# Revit family: C2-260
name_source: partatom
category: Устройства связи
units: mm (PartAtom-declared; Revit-internal decimal feet)

## family parameters
Всегда вертикально = Нет
На основе рабочей плоскости = Нет
Общий = Нет
При загрузке вырезать с полостями = Нет
Размер круглого соединителя = Использовать диаметр
Сохранять ориентацию аннотаций = Нет
Тип детали = Нормальный
Точка расчета площади = Да

## types (5) — shared parameters
=Габариты= = =Габариты=
ADSK_Группирование = 3. Периферийное оборудование
ADSK_Единица измерения = шт.
ADSK_Завод-изготовитель = TemID
ADSK_Количество = 1
URL = https://temid-global.ru
Зона обслуживания_Отступ от прибора = 100 мм
Материал = Светло-чёрный
Текст_цвет = Бледно-жёлтый
Тип геометрии = ВЛ_НО_СС_Геометрия_поворотного_семейства
УГО_Тип = УГО_СС_Контроллер
zero-valued in all types: Отметка по умолчанию

## per-type parameters (varying)
| type | ADSK_Марка | ADSK_Наименование | ADSK_Размер_Высота | ADSK_Размер_Глубина | ADSK_Размер_Ширина | ADSK_Тип | Текст модели |
| C2-260 | C2-260 | IP-контроллер управления двумя дверями | 96 мм | 31 мм | 116 мм | C2-260 | 1 |
| C2-260 Package | C2-260 Package | IP-контроллер управления двумя дверями | 330 мм | 76 мм | 365 мм | C2-260 Package | 1 |
| C3-100 Plus | С3-100 Plus | Сетевой контроллер на одну двухсторонюю дверь | 99 мм | 20 мм | 175 мм | С3-100 Plus | С3-100 |
| C3-200 Plus | C3-200 Plus | Сетевой контроллер для двух двухстороних дверей | 99 мм | 20 мм | 175 мм | C3-200 Plus | С3-100 |
| C3-400 Plus | C3-400 Plus | Сетевой контроллер для четырёх двухстороних дверей | 99 мм | 20 мм | 175 мм | C3-400 Plus | С3-100 |
